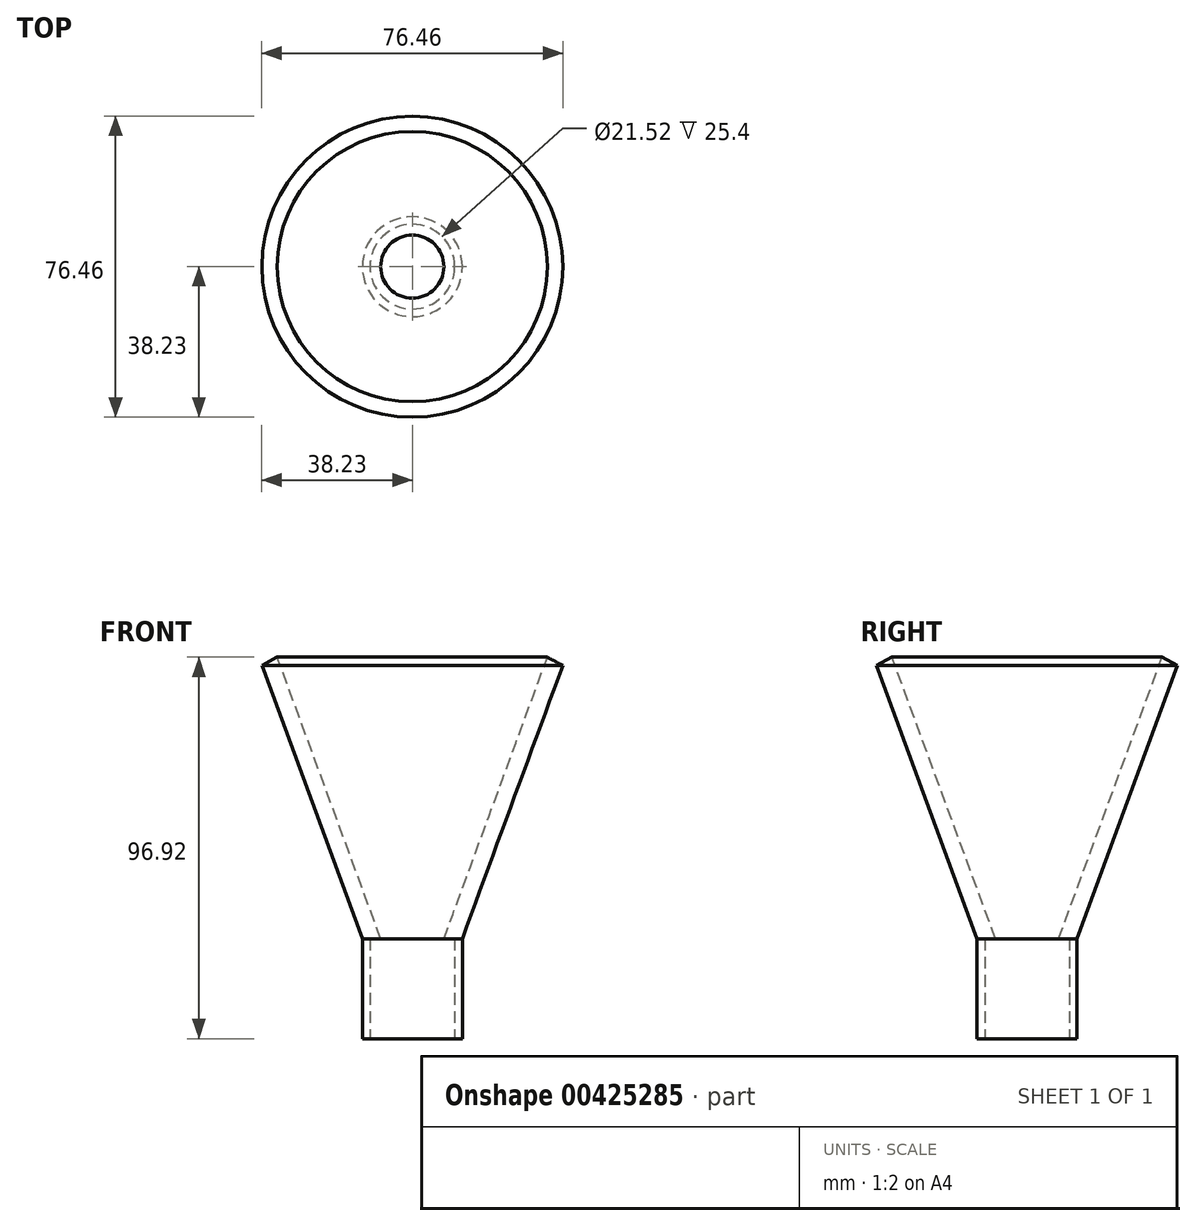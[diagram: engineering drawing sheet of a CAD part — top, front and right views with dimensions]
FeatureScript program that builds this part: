
annotation { "Feature Type Name" : "Feature", "Feature Type Description" : "" }
export const myFeature = defineFeature(function(context is Context, id is Id, definition is map)
    precondition{}
    {
        {
            var Q0;
            Q0=qCreatedBy(makeId("Front.planeOp"),FACE);
            var sketch = newSketch(context, id + "F0", { "sketchPlane" : qUnion([Q0])});
            skLineSegment(sketch, "E0", {"start": v(0, 0) * mm, "end": v(0, -25.4) * mm});
            skLineSegment(sketch, "E1", {"start": v(0, -25.4) * mm, "end": v(12.7, -25.4) * mm});
            skLineSegment(sketch, "E2", {"start": v(12.7, -25.4) * mm, "end": v(12.7, 0) * mm});
            skLineSegment(sketch, "E3", {"start": v(0, 0) * mm, "end": v(8.02, 0) * mm});
            skLineSegment(sketch, "E4", {"start": v(8.02, 0) * mm, "end": v(34.32, 71.52) * mm});
            skLineSegment(sketch, "E5", {"start": v(12.7, 0) * mm, "end": v(38.23, 69.42) * mm});
            skLineSegment(sketch, "E6", {"start": v(38.23, 69.42) * mm, "end": v(34.32, 71.52) * mm});
            skArc(sketch, "E7", {"start": v(0, -25.4) * mm, "mid": v(6.35, -40.92) * mm, "end": v(12.7, -25.4) * mm});
            skSolve(sketch);
        }
        {
            var Q0;
            Q0=makeQuery(id+"F0.imprint","IMPRINT",FACE,{"disambiguationData":[TD([[makeQuery(id+"F0.imprint","IMPRINT",EDGE,{"derivedFrom":sQuery(id+"F0.wireOp",EDGE,"E0")}),1.0]])]});
            var Q1;
            Q1=sQuery(id+"F0.wireOp",EDGE,"E0");
            revolve(context, id + "F1", {"entities" : qUnion([Q0]), "axis" : qUnion([Q1]), "revolveType" : RevolveType.FULL});
        }
        {
            var Q0;
            Q0=makeQuery(id+"F1.opRevolve","SWEPT_FACE",FACE,{"disambiguationData":[OSD([sQuery(id+"F0.wireOp",EDGE,"E1")])]});
            var sketch = newSketch(context, id + "F2", { "sketchPlane" : qUnion([Q0])});
            skCircle(sketch, "E8", {"center": v(0, 0) * mm, "radius": 10.76 * mm});
            skSolve(sketch);
        }
        {
            var Q0;
            Q0 = qSketchRegion(id + "F2", true);
            extrude(context, id + "F3", {"entities" : qUnion([Q0]), "operationType" : NewBodyOperationType.REMOVE, "oppositeDirection" : true, "depth" : 25.4 * mm});
        }
    });
